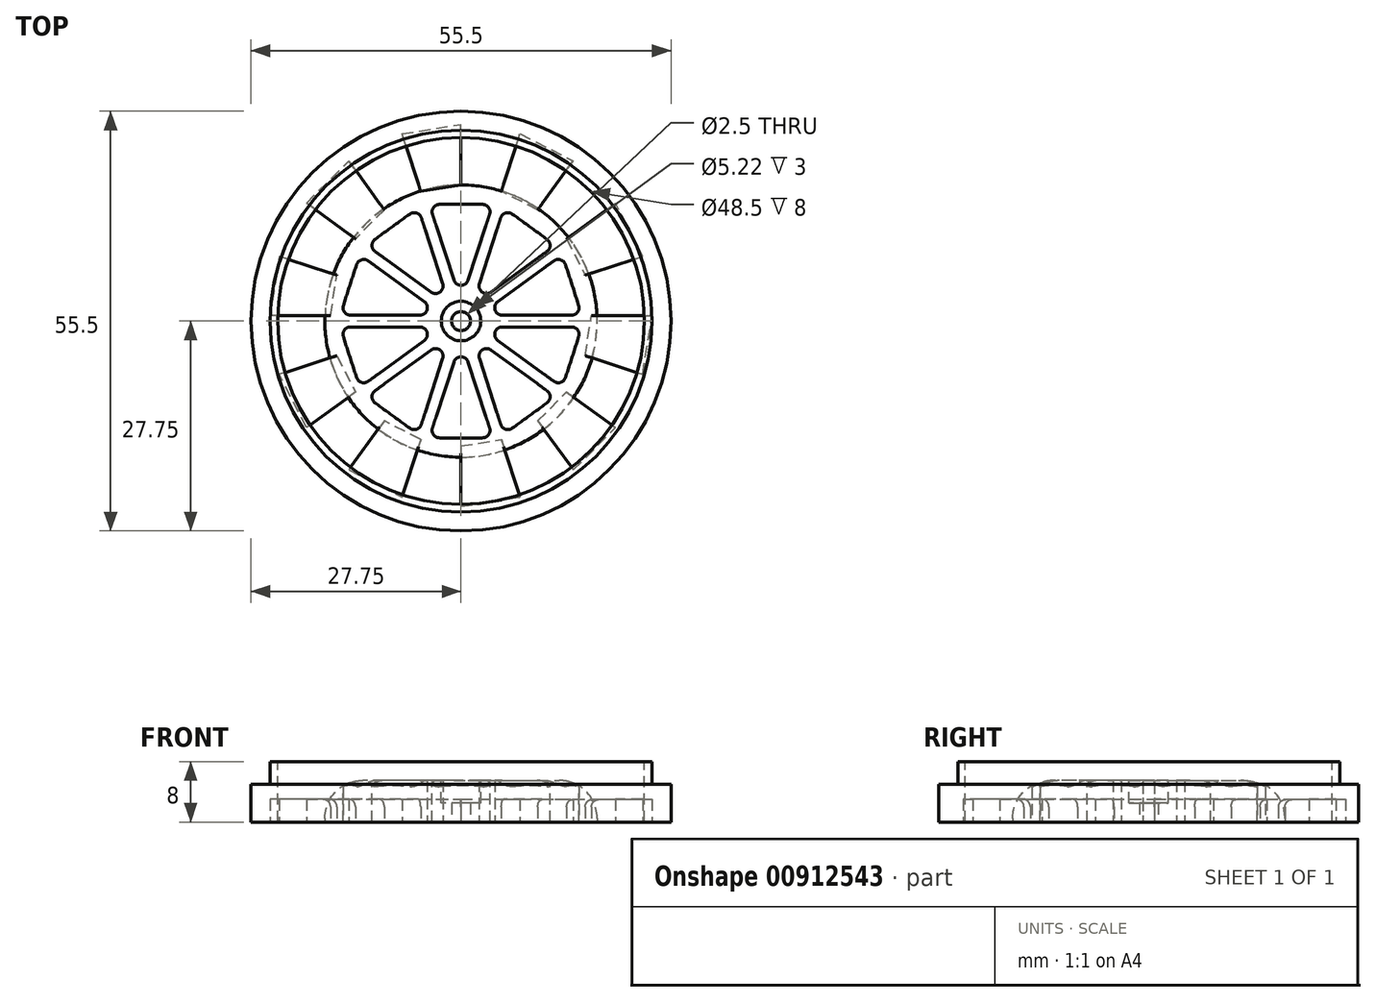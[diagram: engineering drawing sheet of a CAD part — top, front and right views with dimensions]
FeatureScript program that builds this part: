
annotation { "Feature Type Name" : "Feature", "Feature Type Description" : "" }
export const myFeature = defineFeature(function(context is Context, id is Id, definition is map)
    precondition{}
    {
        {
            var Q0;
            Q0=qCreatedBy(makeId("Front.planeOp"),FACE);
            var sketch = newSketch(context, id + "F0", { "sketchPlane" : qUnion([Q0])});
            skLineSegment(sketch, "E0.bottom", {"start": v(-24.25, 0) * mm, "end": v(-25.25, 0) * mm});
            skLineSegment(sketch, "E0.top", {"start": v(-24.25, 8) * mm, "end": v(-25.25, 8) * mm});
            skLineSegment(sketch, "E0.left", {"start": v(-24.25, 0) * mm, "end": v(-24.25, 8) * mm});
            skLineSegment(sketch, "E0.right", {"start": v(-25.25, 0) * mm, "end": v(-25.25, 8) * mm});
            skLineSegment(sketch, "E1.bottom", {"start": v(-27.75, 0) * mm, "end": v(-25.25, 0) * mm});
            skLineSegment(sketch, "E1.top", {"start": v(-27.75, 5) * mm, "end": v(-25.25, 5) * mm});
            skLineSegment(sketch, "E1.left", {"start": v(-27.75, 0) * mm, "end": v(-27.75, 5) * mm});
            skLineSegment(sketch, "E1.right", {"start": v(-25.25, 0) * mm, "end": v(-25.25, 5) * mm});
            skLineSegment(sketch, "E2.MirrorCS", {"start": v(24.25, 0) * mm, "end": v(25.25, 0) * mm});
            skLineSegment(sketch, "E3.MirrorCS", {"start": v(24.25, 8) * mm, "end": v(25.25, 8) * mm});
            skLineSegment(sketch, "E4.MirrorCS", {"start": v(27.75, 0) * mm, "end": v(27.75, 5) * mm});
            skLineSegment(sketch, "E5.MirrorCS", {"start": v(27.75, 5) * mm, "end": v(25.25, 5) * mm});
            skLineSegment(sketch, "E6.MirrorCS", {"start": v(25.25, 0) * mm, "end": v(25.25, 5) * mm});
            skLineSegment(sketch, "E7.MirrorCS", {"start": v(27.75, 0) * mm, "end": v(25.25, 0) * mm});
            skLineSegment(sketch, "E8.MirrorCS", {"start": v(24.25, 0) * mm, "end": v(24.25, 8) * mm});
            skLineSegment(sketch, "E9.MirrorCS", {"start": v(25.25, 0) * mm, "end": v(25.25, 8) * mm});
            skLineSegment(sketch, "E10", {"start": v(0, 21.08) * mm, "end": v(0, -9.2) * mm, "construction": true});
            skSolve(sketch);
        }
        {
            var Q0;
            {var subQ1=sQuery(id+"F0.wireOp",EDGE,"E2.MirrorCS");Q0=makeQuery(id+"F0.imprint","IMPRINT",FACE,{"disambiguationData":[TD([[makeQuery(id+"F0.imprint","IMPRINT",EDGE,{"derivedFrom":subQ1}),1.0]])]});}
            var Q1;
            Q1=makeQuery(id+"F0.imprint","IMPRINT",FACE,{"disambiguationData":[TD([[makeQuery(id+"F0.imprint","IMPRINT",EDGE,{"derivedFrom":sQuery(id+"F0.wireOp",EDGE,"E4.MirrorCS")}),1.0]])]});
            var Q2;
            Q2=sQuery(id+"F0.wireOp",EDGE,"E10");
            revolve(context, id + "F1", {"surfaceOperationType" : NewSurfaceOperationType.NEW, "entities" : qUnion([Q0, Q1]), "axis" : qUnion([Q2]), "revolveType" : RevolveType.FULL});
        }
        {
            var Q0;
            Q0=qCreatedBy(makeId("Top.planeOp"),FACE);
            var sketch = newSketch(context, id + "F2", { "sketchPlane" : qUnion([Q0])});
            skCircle(sketch, "E11", {"center": v(0, 0) * mm, "radius": 18 * mm});
            skCircle(sketch, "E12", {"center": v(0, 0) * mm, "radius": 1.25 * mm});
            skCircle(sketch, "E13", {"center": v(0, 0) * mm, "radius": 2.5 * mm});
            skLineSegment(sketch, "E14", {"start": v(0, 0) * mm, "end": v(0, 18) * mm, "construction": true});
            skLineSegment(sketch, "E15", {"start": v(0, 2.5) * mm, "end": v(-4.2, 15.44) * mm});
            skLineSegment(sketch, "E16", {"start": v(0, 2.5) * mm, "end": v(4.2, 15.44) * mm});
            skLineSegment(sketch, "E17", {"start": v(-4.2, 15.44) * mm, "end": v(4.2, 15.44) * mm});
            skLineSegment(sketch, "E18.1.0", {"start": v(-1.47, 2.02) * mm, "end": v(-12.48, 10.02) * mm});
            skLineSegment(sketch, "E18.1.1", {"start": v(-12.48, 10.02) * mm, "end": v(-5.67, 14.96) * mm});
            skLineSegment(sketch, "E18.1.2", {"start": v(-1.47, 2.02) * mm, "end": v(-5.67, 14.96) * mm});
            skLineSegment(sketch, "E18.2.0", {"start": v(-2.38, 0.77) * mm, "end": v(-15.98, 0.77) * mm});
            skLineSegment(sketch, "E18.2.1", {"start": v(-15.98, 0.77) * mm, "end": v(-13.38, 8.77) * mm});
            skLineSegment(sketch, "E18.2.2", {"start": v(-2.38, 0.77) * mm, "end": v(-13.38, 8.77) * mm});
            skLineSegment(sketch, "E19.1.3.0", {"start": v(-2.38, -0.77) * mm, "end": v(-13.38, -8.77) * mm});
            skLineSegment(sketch, "E19.3.3.0", {"start": v(-13.38, -8.77) * mm, "end": v(-15.98, -0.77) * mm});
            skLineSegment(sketch, "E19.6.3.0", {"start": v(-2.38, -0.77) * mm, "end": v(-15.98, -0.77) * mm});
            skLineSegment(sketch, "E20.1.4.0", {"start": v(-1.47, -2.02) * mm, "end": v(-5.67, -14.96) * mm});
            skLineSegment(sketch, "E20.3.4.0", {"start": v(-5.67, -14.96) * mm, "end": v(-12.48, -10.02) * mm});
            skLineSegment(sketch, "E20.6.4.0", {"start": v(-1.47, -2.02) * mm, "end": v(-12.48, -10.02) * mm});
            skLineSegment(sketch, "E21.1.5.0", {"start": v(0, -2.5) * mm, "end": v(4.2, -15.44) * mm});
            skLineSegment(sketch, "E21.3.5.0", {"start": v(4.2, -15.44) * mm, "end": v(-4.2, -15.44) * mm});
            skLineSegment(sketch, "E21.6.5.0", {"start": v(0, -2.5) * mm, "end": v(-4.2, -15.44) * mm});
            skLineSegment(sketch, "E22.1.6.0", {"start": v(1.47, -2.02) * mm, "end": v(12.48, -10.02) * mm});
            skLineSegment(sketch, "E22.3.6.0", {"start": v(12.48, -10.02) * mm, "end": v(5.67, -14.96) * mm});
            skLineSegment(sketch, "E22.6.6.0", {"start": v(1.47, -2.02) * mm, "end": v(5.67, -14.96) * mm});
            skLineSegment(sketch, "E23.1.7.0", {"start": v(2.38, -0.77) * mm, "end": v(15.98, -0.77) * mm});
            skLineSegment(sketch, "E23.3.7.0", {"start": v(15.98, -0.77) * mm, "end": v(13.38, -8.77) * mm});
            skLineSegment(sketch, "E23.6.7.0", {"start": v(2.38, -0.77) * mm, "end": v(13.38, -8.77) * mm});
            skLineSegment(sketch, "E24.1.8.0", {"start": v(2.38, 0.77) * mm, "end": v(13.38, 8.77) * mm});
            skLineSegment(sketch, "E24.3.8.0", {"start": v(13.38, 8.77) * mm, "end": v(15.98, 0.77) * mm});
            skLineSegment(sketch, "E24.6.8.0", {"start": v(2.38, 0.77) * mm, "end": v(15.98, 0.77) * mm});
            skLineSegment(sketch, "E25.1.9.0", {"start": v(1.47, 2.02) * mm, "end": v(5.67, 14.96) * mm});
            skLineSegment(sketch, "E25.3.9.0", {"start": v(5.67, 14.96) * mm, "end": v(12.48, 10.02) * mm});
            skLineSegment(sketch, "E25.6.9.0", {"start": v(1.47, 2.02) * mm, "end": v(12.48, 10.02) * mm});
            skSolve(sketch);
        }
        {
            var Q0;
            Q0 = qSketchRegion(id + "F2", true);
            var Q1;
            Q1=makeQuery(id+"F2.imprint","IMPRINT",FACE,{"disambiguationData":[TD([[makeQuery(id+"F2.imprint","IMPRINT",EDGE,{"derivedFrom":sQuery(id+"F2.wireOp",EDGE,"E12")}),-1.0]])]});
            extrude(context, id + "F3", {"entities" : qUnion([Q0, Q1]), "depth" : 5.5 * mm, "offsetDistance" : 25 * mm});
        }
        {
            var Q0;
            Q0=qCreatedBy(makeId("Top.planeOp"),FACE);
            var sketch = newSketch(context, id + "F4", { "sketchPlane" : qUnion([Q0])});
            skPoint(sketch, "E26", {"position": v(0, 18) * mm});
            skLineSegment(sketch, "E27", {"start": v(0, 18) * mm, "end": v(0, 26) * mm});
            skLineSegment(sketch, "E28.1.0", {"start": v(-5.33, 17.16) * mm, "end": v(-7.8, 24.76) * mm});
            skLineSegment(sketch, "E28.2.0", {"start": v(-10.14, 14.7) * mm, "end": v(-14.84, 21.18) * mm});
            skLineSegment(sketch, "E28.3.0", {"start": v(-13.96, 10.89) * mm, "end": v(-20.43, 15.6) * mm});
            skLineSegment(sketch, "E28.4.0", {"start": v(-16.4, 6.08) * mm, "end": v(-24.01, 8.55) * mm});
            skLineSegment(sketch, "E28.5.0", {"start": v(-17.25, 0.75) * mm, "end": v(-25.25, 0.75) * mm});
            skLineSegment(sketch, "E28.6.0", {"start": v(-16.4, -4.58) * mm, "end": v(-24.01, -7.05) * mm});
            skLineSegment(sketch, "E28.7.0", {"start": v(-13.96, -9.39) * mm, "end": v(-20.43, -14.1) * mm});
            skLineSegment(sketch, "E28.8.0", {"start": v(-10.14, -13.2) * mm, "end": v(-14.84, -19.68) * mm});
            skLineSegment(sketch, "E28.9.0", {"start": v(-5.33, -15.66) * mm, "end": v(-7.8, -23.26) * mm});
            skPoint(sketch, "E28.center", {"position": v(0, 0.75) * mm});
            skLineSegment(sketch, "E29.1.10.0", {"start": v(0, -16.5) * mm, "end": v(0, -24.5) * mm});
            skLineSegment(sketch, "E29.1.11.0", {"start": v(5.33, -15.66) * mm, "end": v(7.8, -23.26) * mm});
            skLineSegment(sketch, "E29.1.12.0", {"start": v(10.14, -13.2) * mm, "end": v(14.84, -19.68) * mm});
            skLineSegment(sketch, "E29.1.13.0", {"start": v(13.96, -9.39) * mm, "end": v(20.43, -14.1) * mm});
            skLineSegment(sketch, "E29.1.14.0", {"start": v(16.4, -4.58) * mm, "end": v(24.01, -7.05) * mm});
            skLineSegment(sketch, "E29.1.15.0", {"start": v(17.25, 0.75) * mm, "end": v(25.25, 0.75) * mm});
            skLineSegment(sketch, "E29.1.16.0", {"start": v(16.4, 6.08) * mm, "end": v(24.01, 8.55) * mm});
            skLineSegment(sketch, "E29.1.17.0", {"start": v(13.96, 10.89) * mm, "end": v(20.43, 15.6) * mm});
            skLineSegment(sketch, "E29.1.18.0", {"start": v(10.14, 14.7) * mm, "end": v(14.84, 21.18) * mm});
            skLineSegment(sketch, "E29.1.19.0", {"start": v(5.33, 17.16) * mm, "end": v(7.8, 24.76) * mm});
            skLineSegment(sketch, "E30", {"start": v(-5.33, 17.16) * mm, "end": v(0, 18) * mm});
            skLineSegment(sketch, "E31", {"start": v(-7.8, 24.76) * mm, "end": v(0, 26) * mm});
            skLineSegment(sketch, "E32", {"start": v(-10.14, 14.7) * mm, "end": v(-13.96, 10.89) * mm});
            skLineSegment(sketch, "E33", {"start": v(-20.43, 15.6) * mm, "end": v(-14.84, 21.18) * mm});
            skLineSegment(sketch, "E34", {"start": v(-24.01, 8.55) * mm, "end": v(-25.25, 0.75) * mm});
            skLineSegment(sketch, "E35", {"start": v(-17.25, 0.75) * mm, "end": v(-16.4, 6.08) * mm});
            skLineSegment(sketch, "E36", {"start": v(-16.4, -4.58) * mm, "end": v(-13.96, -9.39) * mm});
            skLineSegment(sketch, "E37", {"start": v(-20.43, -14.1) * mm, "end": v(-24.01, -7.05) * mm});
            skLineSegment(sketch, "E38", {"start": v(-14.84, -19.68) * mm, "end": v(-7.8, -23.26) * mm});
            skLineSegment(sketch, "E39", {"start": v(-5.33, -15.66) * mm, "end": v(-10.14, -13.2) * mm});
            skLineSegment(sketch, "E40", {"start": v(0, -16.5) * mm, "end": v(5.33, -15.66) * mm});
            skLineSegment(sketch, "E41", {"start": v(0, -24.5) * mm, "end": v(7.8, -23.26) * mm});
            skLineSegment(sketch, "E42", {"start": v(14.84, -19.68) * mm, "end": v(20.43, -14.1) * mm});
            skLineSegment(sketch, "E43", {"start": v(10.14, -13.2) * mm, "end": v(13.96, -9.39) * mm});
            skLineSegment(sketch, "E44", {"start": v(16.4, -4.58) * mm, "end": v(17.25, 0.75) * mm});
            skLineSegment(sketch, "E45", {"start": v(24.01, -7.05) * mm, "end": v(25.25, 0.75) * mm});
            skLineSegment(sketch, "E46", {"start": v(24.01, 8.55) * mm, "end": v(20.43, 15.6) * mm});
            skLineSegment(sketch, "E47", {"start": v(13.96, 10.89) * mm, "end": v(16.4, 6.08) * mm});
            skLineSegment(sketch, "E48", {"start": v(10.14, 14.7) * mm, "end": v(5.33, 17.16) * mm});
            skLineSegment(sketch, "E49", {"start": v(7.8, 24.76) * mm, "end": v(14.84, 21.18) * mm});
            skSolve(sketch);
        }
        {
            var Q0;
            Q0=makeQuery(id+"F4.imprint","IMPRINT",FACE,{"disambiguationData":[TD([[makeQuery(id+"F4.imprint","IMPRINT",EDGE,{"derivedFrom":sQuery(id+"F4.wireOp",EDGE,"E28.2.0")}),1.0]])]});
            var Q1;
            Q1=makeQuery(id+"F4.imprint","IMPRINT",FACE,{"disambiguationData":[TD([[makeQuery(id+"F4.imprint","IMPRINT",EDGE,{"derivedFrom":sQuery(id+"F4.wireOp",EDGE,"E27")}),1.0]])]});
            var Q2;
            Q2=makeQuery(id+"F4.imprint","IMPRINT",FACE,{"disambiguationData":[TD([[makeQuery(id+"F4.imprint","IMPRINT",EDGE,{"derivedFrom":sQuery(id+"F4.wireOp",EDGE,"E29.1.18.0")}),1.0]])]});
            var Q3;
            Q3=makeQuery(id+"F4.imprint","IMPRINT",FACE,{"disambiguationData":[TD([[makeQuery(id+"F4.imprint","IMPRINT",EDGE,{"derivedFrom":sQuery(id+"F4.wireOp",EDGE,"E29.1.16.0")}),1.0]])]});
            var Q4;
            Q4=makeQuery(id+"F4.imprint","IMPRINT",FACE,{"disambiguationData":[TD([[makeQuery(id+"F4.imprint","IMPRINT",EDGE,{"derivedFrom":sQuery(id+"F4.wireOp",EDGE,"E29.1.14.0")}),1.0]])]});
            var Q5;
            Q5=makeQuery(id+"F4.imprint","IMPRINT",FACE,{"disambiguationData":[TD([[makeQuery(id+"F4.imprint","IMPRINT",EDGE,{"derivedFrom":sQuery(id+"F4.wireOp",EDGE,"E29.1.12.0")}),1.0]])]});
            var Q6;
            Q6=makeQuery(id+"F4.imprint","IMPRINT",FACE,{"disambiguationData":[TD([[makeQuery(id+"F4.imprint","IMPRINT",EDGE,{"derivedFrom":sQuery(id+"F4.wireOp",EDGE,"E29.1.10.0")}),1.0]])]});
            var Q7;
            Q7=makeQuery(id+"F4.imprint","IMPRINT",FACE,{"disambiguationData":[TD([[makeQuery(id+"F4.imprint","IMPRINT",EDGE,{"derivedFrom":sQuery(id+"F4.wireOp",EDGE,"E28.8.0")}),1.0]])]});
            var Q8;
            Q8=makeQuery(id+"F4.imprint","IMPRINT",FACE,{"disambiguationData":[TD([[makeQuery(id+"F4.imprint","IMPRINT",EDGE,{"derivedFrom":sQuery(id+"F4.wireOp",EDGE,"E28.6.0")}),1.0]])]});
            var Q9;
            Q9=makeQuery(id+"F4.imprint","IMPRINT",FACE,{"disambiguationData":[TD([[makeQuery(id+"F4.imprint","IMPRINT",EDGE,{"derivedFrom":sQuery(id+"F4.wireOp",EDGE,"E28.4.0")}),1.0]])]});
            extrude(context, id + "F5", {"entities" : qUnion([Q0, Q1, Q2, Q3, Q4, Q5, Q6, Q7, Q8, Q9]), "depth" : 3 * mm, "offsetDistance" : 25 * mm});
        }
        {
            var Q0;
            Q0=makeQuery(id+"F3.opExtrude","SWEPT_EDGE",EDGE,{"disambiguationData":[OSD([sQuery(id+"F2.wireOp",EDGE,"E18.1.1"),sQuery(id+"F2.wireOp",EDGE,"E18.1.2")])]});
            var Q1;
            Q1=makeQuery(id+"F3.opExtrude","SWEPT_EDGE",EDGE,{"disambiguationData":[OSD([sQuery(id+"F2.wireOp",EDGE,"E16"),sQuery(id+"F2.wireOp",EDGE,"E17")])]});
            var Q2;
            Q2=makeQuery(id+"F3.opExtrude","SWEPT_EDGE",EDGE,{"disambiguationData":[OSD([sQuery(id+"F2.wireOp",EDGE,"E25.3.9.0"),sQuery(id+"F2.wireOp",EDGE,"E25.6.9.0")])]});
            var Q3;
            Q3=makeQuery(id+"F3.opExtrude","SWEPT_EDGE",EDGE,{"disambiguationData":[OSD([sQuery(id+"F2.wireOp",EDGE,"E24.3.8.0"),sQuery(id+"F2.wireOp",EDGE,"E24.6.8.0")])]});
            var Q4;
            Q4=makeQuery(id+"F3.opExtrude","SWEPT_EDGE",EDGE,{"disambiguationData":[OSD([sQuery(id+"F2.wireOp",EDGE,"E23.3.7.0"),sQuery(id+"F2.wireOp",EDGE,"E23.6.7.0")])]});
            var Q5;
            Q5=makeQuery(id+"F3.opExtrude","SWEPT_EDGE",EDGE,{"disambiguationData":[OSD([sQuery(id+"F2.wireOp",EDGE,"E22.3.6.0"),sQuery(id+"F2.wireOp",EDGE,"E22.6.6.0")])]});
            var Q6;
            Q6=makeQuery(id+"F3.opExtrude","SWEPT_EDGE",EDGE,{"disambiguationData":[OSD([sQuery(id+"F2.wireOp",EDGE,"E21.3.5.0"),sQuery(id+"F2.wireOp",EDGE,"E21.6.5.0")])]});
            var Q7;
            Q7=makeQuery(id+"F3.opExtrude","SWEPT_EDGE",EDGE,{"disambiguationData":[OSD([sQuery(id+"F2.wireOp",EDGE,"E20.3.4.0"),sQuery(id+"F2.wireOp",EDGE,"E20.6.4.0")])]});
            var Q8;
            Q8=makeQuery(id+"F3.opExtrude","SWEPT_EDGE",EDGE,{"disambiguationData":[OSD([sQuery(id+"F2.wireOp",EDGE,"E19.3.3.0"),sQuery(id+"F2.wireOp",EDGE,"E19.6.3.0")])]});
            var Q9;
            Q9=makeQuery(id+"F3.opExtrude","SWEPT_EDGE",EDGE,{"disambiguationData":[OSD([sQuery(id+"F2.wireOp",EDGE,"E18.2.1"),sQuery(id+"F2.wireOp",EDGE,"E18.2.2")])]});
            var Q10;
            Q10=makeQuery(id+"F3.opExtrude","SWEPT_EDGE",EDGE,{"disambiguationData":[OSD([sQuery(id+"F2.wireOp",EDGE,"E24.1.8.0"),sQuery(id+"F2.wireOp",EDGE,"E24.3.8.0")])]});
            var Q11;
            Q11=makeQuery(id+"F3.opExtrude","SWEPT_EDGE",EDGE,{"disambiguationData":[OSD([sQuery(id+"F2.wireOp",EDGE,"E25.1.9.0"),sQuery(id+"F2.wireOp",EDGE,"E25.3.9.0")])]});
            var Q12;
            Q12=makeQuery(id+"F3.opExtrude","SWEPT_EDGE",EDGE,{"disambiguationData":[OSD([sQuery(id+"F2.wireOp",EDGE,"E15"),sQuery(id+"F2.wireOp",EDGE,"E17")])]});
            var Q13;
            Q13=makeQuery(id+"F3.opExtrude","SWEPT_EDGE",EDGE,{"disambiguationData":[OSD([sQuery(id+"F2.wireOp",EDGE,"E18.1.0"),sQuery(id+"F2.wireOp",EDGE,"E18.1.1")])]});
            var Q14;
            Q14=makeQuery(id+"F3.opExtrude","SWEPT_EDGE",EDGE,{"disambiguationData":[OSD([sQuery(id+"F2.wireOp",EDGE,"E18.2.0"),sQuery(id+"F2.wireOp",EDGE,"E18.2.1")])]});
            var Q15;
            Q15=makeQuery(id+"F3.opExtrude","SWEPT_EDGE",EDGE,{"disambiguationData":[OSD([sQuery(id+"F2.wireOp",EDGE,"E19.1.3.0"),sQuery(id+"F2.wireOp",EDGE,"E19.3.3.0")])]});
            var Q16;
            Q16=makeQuery(id+"F3.opExtrude","SWEPT_EDGE",EDGE,{"disambiguationData":[OSD([sQuery(id+"F2.wireOp",EDGE,"E20.1.4.0"),sQuery(id+"F2.wireOp",EDGE,"E20.3.4.0")])]});
            var Q17;
            Q17=makeQuery(id+"F3.opExtrude","SWEPT_EDGE",EDGE,{"disambiguationData":[OSD([sQuery(id+"F2.wireOp",EDGE,"E21.1.5.0"),sQuery(id+"F2.wireOp",EDGE,"E21.3.5.0")])]});
            var Q18;
            Q18=makeQuery(id+"F3.opExtrude","SWEPT_EDGE",EDGE,{"disambiguationData":[OSD([sQuery(id+"F2.wireOp",EDGE,"E22.1.6.0"),sQuery(id+"F2.wireOp",EDGE,"E22.3.6.0")])]});
            var Q19;
            Q19=makeQuery(id+"F3.opExtrude","SWEPT_EDGE",EDGE,{"disambiguationData":[OSD([sQuery(id+"F2.wireOp",EDGE,"E23.1.7.0"),sQuery(id+"F2.wireOp",EDGE,"E23.3.7.0")])]});
            fillet(context, id + "F6", {"entities" : qUnion([Q0, Q1, Q2, Q3, Q4, Q5, Q6, Q7, Q8, Q9, Q10, Q11, Q12, Q13, Q14, Q15, Q16, Q17, Q18, Q19]), "radius" : 1 * mm, "tangentPropagation" : true, "allowEdgeOverflow" : false});
        }
        {
            var Q0;
            Q0=makeQuery(id+"F5.opExtrude","CAP_EDGE",EDGE,{"disambiguationData":[OSD([sQuery(id+"F4.wireOp",EDGE,"E30")])],"isStart":false});
            var Q1;
            Q1=makeQuery(id+"F5.opExtrude","CAP_EDGE",EDGE,{"disambiguationData":[OSD([sQuery(id+"F4.wireOp",EDGE,"E32")])],"isStart":false});
            var Q2;
            Q2=makeQuery(id+"F5.opExtrude","CAP_EDGE",EDGE,{"disambiguationData":[OSD([sQuery(id+"F4.wireOp",EDGE,"E35")])],"isStart":false});
            var Q3;
            Q3=makeQuery(id+"F5.opExtrude","CAP_EDGE",EDGE,{"disambiguationData":[OSD([sQuery(id+"F4.wireOp",EDGE,"E36")])],"isStart":false});
            var Q4;
            Q4=makeQuery(id+"F5.opExtrude","CAP_EDGE",EDGE,{"disambiguationData":[OSD([sQuery(id+"F4.wireOp",EDGE,"E39")])],"isStart":false});
            var Q5;
            Q5=makeQuery(id+"F5.opExtrude","CAP_EDGE",EDGE,{"disambiguationData":[OSD([sQuery(id+"F4.wireOp",EDGE,"E40")])],"isStart":false});
            var Q6;
            Q6=makeQuery(id+"F5.opExtrude","CAP_EDGE",EDGE,{"disambiguationData":[OSD([sQuery(id+"F4.wireOp",EDGE,"E43")])],"isStart":false});
            var Q7;
            Q7=makeQuery(id+"F5.opExtrude","CAP_EDGE",EDGE,{"disambiguationData":[OSD([sQuery(id+"F4.wireOp",EDGE,"E44")])],"isStart":false});
            var Q8;
            Q8=makeQuery(id+"F5.opExtrude","CAP_EDGE",EDGE,{"disambiguationData":[OSD([sQuery(id+"F4.wireOp",EDGE,"E47")])],"isStart":false});
            var Q9;
            Q9=makeQuery(id+"F5.opExtrude","CAP_EDGE",EDGE,{"disambiguationData":[OSD([sQuery(id+"F4.wireOp",EDGE,"E48")])],"isStart":false});
            fillet(context, id + "F7", {"entities" : qUnion([Q0, Q1, Q2, Q3, Q4, Q5, Q6, Q7, Q8, Q9]), "radius" : 1 * mm, "tangentPropagation" : true, "allowEdgeOverflow" : false});
        }
        {
            var Q0;
            Q0=makeQuery(id+"F3.opExtrude","SWEPT_EDGE",EDGE,{"disambiguationData":[OSD([sQuery(id+"F2.wireOp",EDGE,"E13"),sQuery(id+"F2.wireOp",EDGE,"E18.2.0"),sQuery(id+"F2.wireOp",EDGE,"E18.2.2")])]});
            var Q1;
            Q1=makeQuery(id+"F3.opExtrude","SWEPT_EDGE",EDGE,{"disambiguationData":[OSD([sQuery(id+"F2.wireOp",EDGE,"E13"),sQuery(id+"F2.wireOp",EDGE,"E19.1.3.0"),sQuery(id+"F2.wireOp",EDGE,"E19.6.3.0")])]});
            var Q2;
            Q2=makeQuery(id+"F3.opExtrude","SWEPT_EDGE",EDGE,{"disambiguationData":[OSD([sQuery(id+"F2.wireOp",EDGE,"E13"),sQuery(id+"F2.wireOp",EDGE,"E20.1.4.0"),sQuery(id+"F2.wireOp",EDGE,"E20.6.4.0")])]});
            var Q3;
            Q3=makeQuery(id+"F3.opExtrude","SWEPT_EDGE",EDGE,{"disambiguationData":[OSD([sQuery(id+"F2.wireOp",EDGE,"E13"),sQuery(id+"F2.wireOp",EDGE,"E21.1.5.0"),sQuery(id+"F2.wireOp",EDGE,"E21.6.5.0")])]});
            var Q4;
            Q4=makeQuery(id+"F3.opExtrude","SWEPT_EDGE",EDGE,{"disambiguationData":[OSD([sQuery(id+"F2.wireOp",EDGE,"E13"),sQuery(id+"F2.wireOp",EDGE,"E22.1.6.0"),sQuery(id+"F2.wireOp",EDGE,"E22.6.6.0")])]});
            var Q5;
            Q5=makeQuery(id+"F3.opExtrude","SWEPT_EDGE",EDGE,{"disambiguationData":[OSD([sQuery(id+"F2.wireOp",EDGE,"E13"),sQuery(id+"F2.wireOp",EDGE,"E23.1.7.0"),sQuery(id+"F2.wireOp",EDGE,"E23.6.7.0")])]});
            var Q6;
            Q6=makeQuery(id+"F3.opExtrude","SWEPT_EDGE",EDGE,{"disambiguationData":[OSD([sQuery(id+"F2.wireOp",EDGE,"E13"),sQuery(id+"F2.wireOp",EDGE,"E24.1.8.0"),sQuery(id+"F2.wireOp",EDGE,"E24.6.8.0")])]});
            var Q7;
            Q7=makeQuery(id+"F3.opExtrude","SWEPT_EDGE",EDGE,{"disambiguationData":[OSD([sQuery(id+"F2.wireOp",EDGE,"E13"),sQuery(id+"F2.wireOp",EDGE,"E25.1.9.0"),sQuery(id+"F2.wireOp",EDGE,"E25.6.9.0")])]});
            var Q8;
            Q8=makeQuery(id+"F3.opExtrude","SWEPT_EDGE",EDGE,{"disambiguationData":[OSD([sQuery(id+"F2.wireOp",EDGE,"E13"),sQuery(id+"F2.wireOp",EDGE,"E15"),sQuery(id+"F2.wireOp",EDGE,"E16")])]});
            var Q9;
            Q9=makeQuery(id+"F3.opExtrude","SWEPT_EDGE",EDGE,{"disambiguationData":[OSD([sQuery(id+"F2.wireOp",EDGE,"E13"),sQuery(id+"F2.wireOp",EDGE,"E18.1.0"),sQuery(id+"F2.wireOp",EDGE,"E18.1.2")])]});
            fillet(context, id + "F8", {"entities" : qUnion([Q0, Q1, Q2, Q3, Q4, Q5, Q6, Q7, Q8, Q9]), "radius" : 1 * mm, "tangentPropagation" : true, "allowEdgeOverflow" : false});
        }
        {
            var Q0;
            Q0=makeQuery(id+"F3.opExtrude","CAP_FACE",FACE,{"disambiguationData":[OSD([sQuery(id+"F2.wireOp",EDGE,"E11"),sQuery(id+"F2.wireOp",EDGE,"E12"),sQuery(id+"F2.wireOp",EDGE,"E15"),sQuery(id+"F2.wireOp",EDGE,"E16"),sQuery(id+"F2.wireOp",EDGE,"E17"),sQuery(id+"F2.wireOp",EDGE,"E18.1.0"),sQuery(id+"F2.wireOp",EDGE,"E18.1.1"),sQuery(id+"F2.wireOp",EDGE,"E18.1.2"),sQuery(id+"F2.wireOp",EDGE,"E18.2.0"),sQuery(id+"F2.wireOp",EDGE,"E18.2.1"),sQuery(id+"F2.wireOp",EDGE,"E18.2.2"),sQuery(id+"F2.wireOp",EDGE,"E19.1.3.0"),sQuery(id+"F2.wireOp",EDGE,"E19.3.3.0"),sQuery(id+"F2.wireOp",EDGE,"E19.6.3.0"),sQuery(id+"F2.wireOp",EDGE,"E20.1.4.0"),sQuery(id+"F2.wireOp",EDGE,"E20.3.4.0"),sQuery(id+"F2.wireOp",EDGE,"E20.6.4.0"),sQuery(id+"F2.wireOp",EDGE,"E21.1.5.0"),sQuery(id+"F2.wireOp",EDGE,"E21.3.5.0"),sQuery(id+"F2.wireOp",EDGE,"E21.6.5.0"),sQuery(id+"F2.wireOp",EDGE,"E22.1.6.0"),sQuery(id+"F2.wireOp",EDGE,"E22.3.6.0"),sQuery(id+"F2.wireOp",EDGE,"E22.6.6.0"),sQuery(id+"F2.wireOp",EDGE,"E23.1.7.0"),sQuery(id+"F2.wireOp",EDGE,"E23.3.7.0"),sQuery(id+"F2.wireOp",EDGE,"E23.6.7.0"),sQuery(id+"F2.wireOp",EDGE,"E24.1.8.0"),sQuery(id+"F2.wireOp",EDGE,"E24.3.8.0"),sQuery(id+"F2.wireOp",EDGE,"E24.6.8.0"),sQuery(id+"F2.wireOp",EDGE,"E25.1.9.0"),sQuery(id+"F2.wireOp",EDGE,"E25.3.9.0"),sQuery(id+"F2.wireOp",EDGE,"E25.6.9.0")])],"isStart":false});
            var sketch = newSketch(context, id + "F9", { "sketchPlane" : qUnion([Q0])});
            skCircle(sketch, "E50", {"center": v(0, 0) * mm, "radius": 2.6 * mm});
            skSolve(sketch);
        }
        {
            var Q0;
            Q0=makeQuery(id+"F9.imprint","IMPRINT",FACE,{"disambiguationData":[TD([[makeQuery(id+"F9.imprint","IMPRINT",EDGE,{"derivedFrom":sQuery(id+"F9.wireOp",EDGE,"E50")}),1.0]])]});
            extrude(context, id + "F10", {"entities" : qUnion([Q0]), "operationType" : NewBodyOperationType.REMOVE, "oppositeDirection" : true, "depth" : 3 * mm, "offsetDistance" : 25 * mm});
        }
        {
            var Q0;
            Q0=makeQuery(id+"F3.opExtrude","CAP_EDGE",EDGE,{"disambiguationData":[OSD([sQuery(id+"F2.wireOp",EDGE,"E11")])],"isStart":false});
            fillet(context, id + "F11", {"entities" : qUnion([Q0]), "radius" : 5 * mm, "tangentPropagation" : true, "allowEdgeOverflow" : false});
        }
    });
